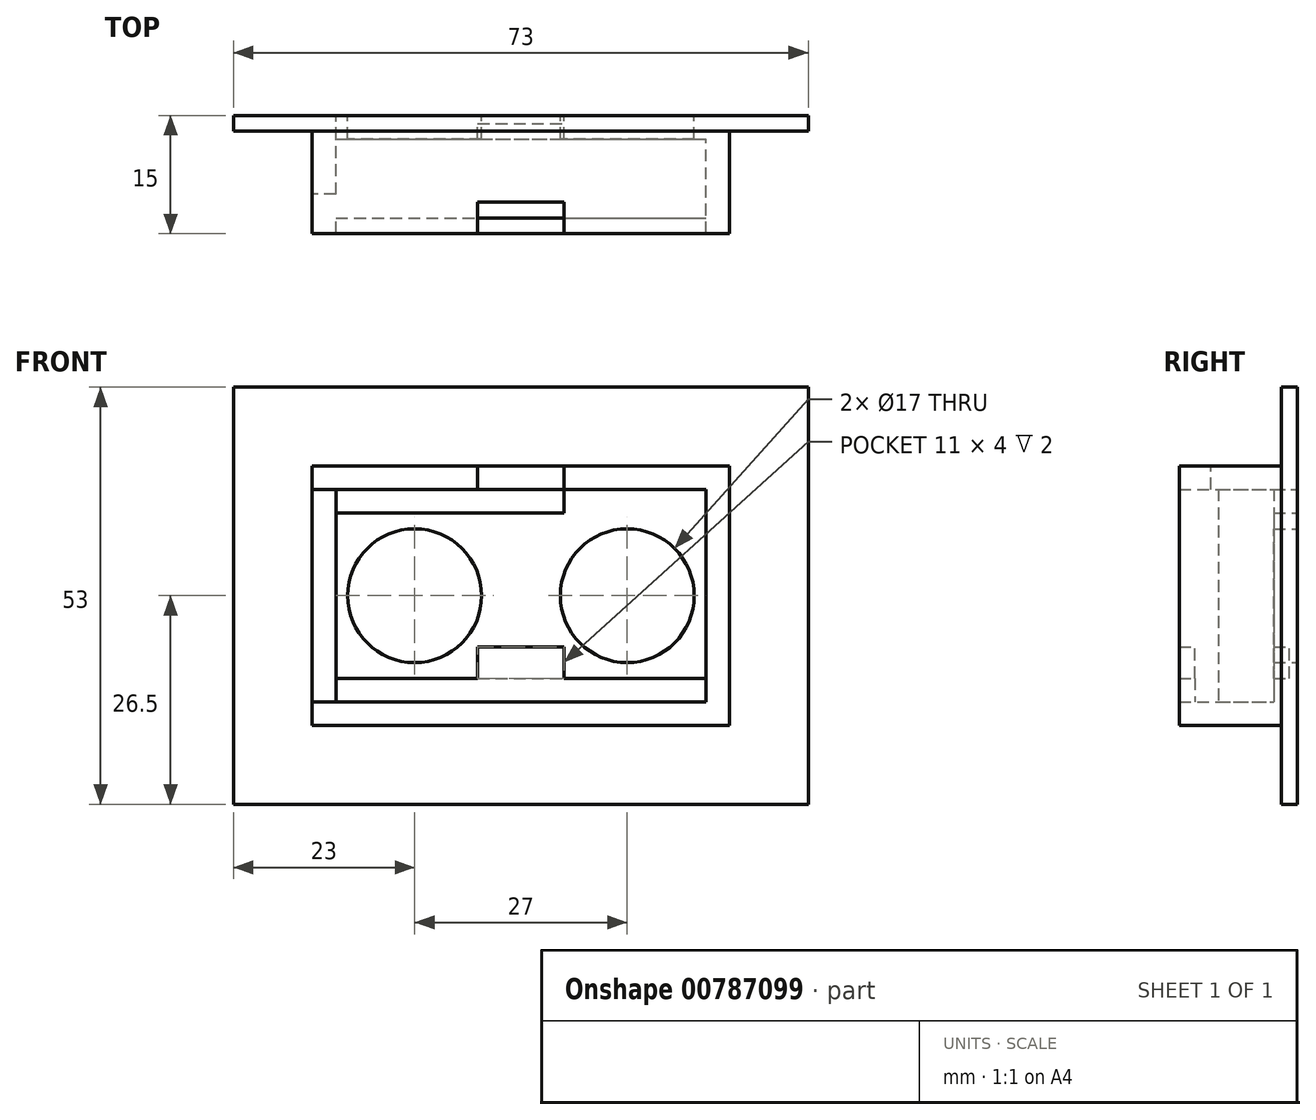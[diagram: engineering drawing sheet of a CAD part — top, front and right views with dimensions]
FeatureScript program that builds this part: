
annotation { "Feature Type Name" : "Feature", "Feature Type Description" : "" }
export const myFeature = defineFeature(function(context is Context, id is Id, definition is map)
    precondition{}
    {
        {
            var Q0;
            Q0=qCreatedBy(makeId("Front.planeOp"),FACE);
            var sketch = newSketch(context, id + "F0", { "sketchPlane" : qUnion([Q0])});
            skLineSegment(sketch, "E0.bottom", {"start": v(-23.5, 13.5) * mm, "end": v(23.5, 13.5) * mm});
            skLineSegment(sketch, "E0.top", {"start": v(-23.5, -13.5) * mm, "end": v(23.5, -13.5) * mm});
            skLineSegment(sketch, "E0.left", {"start": v(-23.5, 13.5) * mm, "end": v(-23.5, -13.5) * mm});
            skLineSegment(sketch, "E0.right", {"start": v(23.5, 13.5) * mm, "end": v(23.5, -13.5) * mm});
            skPoint(sketch, "E0.middle", {"position": v(0, 0) * mm});
            skPoint(sketch, "E1", {"position": v(-13.5, 0) * mm});
            skCircle(sketch, "E2", {"center": v(-13.5, 0) * mm, "radius": 8.5 * mm});
            skCircle(sketch, "E3.MirrorC", {"center": v(13.5, 0) * mm, "radius": 8.5 * mm});
            skPoint(sketch, "E4.positionSnap0", {"position": v(0, -13.5) * mm});
            skLineSegment(sketch, "E5.bottom", {"start": v(-5.5, -10.5) * mm, "end": v(5.5, -10.5) * mm});
            skLineSegment(sketch, "E5.top", {"start": v(-5.5, -6.5) * mm, "end": v(5.5, -6.5) * mm});
            skLineSegment(sketch, "E5.left", {"start": v(-5.5, -10.5) * mm, "end": v(-5.5, -6.5) * mm});
            skLineSegment(sketch, "E5.right", {"start": v(5.5, -10.5) * mm, "end": v(5.5, -6.5) * mm});
            skLineSegment(sketch, "E6.bottom", {"start": v(-23.5, 13.5) * mm, "end": v(-26.5, 13.5) * mm});
            skLineSegment(sketch, "E6.top", {"start": v(-23.5, -13.5) * mm, "end": v(-26.5, -13.5) * mm});
            skLineSegment(sketch, "E6.right", {"start": v(-26.5, 13.5) * mm, "end": v(-26.5, -13.5) * mm});
            skLineSegment(sketch, "E7.bottom", {"start": v(23.5, 13.5) * mm, "end": v(26.5, 13.5) * mm});
            skLineSegment(sketch, "E7.top", {"start": v(23.5, -13.5) * mm, "end": v(26.5, -13.5) * mm});
            skLineSegment(sketch, "E7.right", {"start": v(26.5, 13.5) * mm, "end": v(26.5, -13.5) * mm});
            skLineSegment(sketch, "E8.bottom", {"start": v(-26.5, 13.5) * mm, "end": v(26.5, 13.5) * mm});
            skLineSegment(sketch, "E8.top", {"start": v(-26.5, 16.5) * mm, "end": v(26.5, 16.5) * mm});
            skLineSegment(sketch, "E8.left", {"start": v(-26.5, 13.5) * mm, "end": v(-26.5, 16.5) * mm});
            skLineSegment(sketch, "E8.right", {"start": v(26.5, 13.5) * mm, "end": v(26.5, 16.5) * mm});
            skLineSegment(sketch, "E9.bottom", {"start": v(-26.5, -13.5) * mm, "end": v(26.5, -13.5) * mm});
            skLineSegment(sketch, "E9.top", {"start": v(-26.5, -16.5) * mm, "end": v(26.5, -16.5) * mm});
            skLineSegment(sketch, "E9.left", {"start": v(-26.5, -13.5) * mm, "end": v(-26.5, -16.5) * mm});
            skLineSegment(sketch, "E9.right", {"start": v(26.5, -13.5) * mm, "end": v(26.5, -16.5) * mm});
            skLineSegment(sketch, "E10.bottom", {"start": v(-5.5, -13.5) * mm, "end": v(5.5, -13.5) * mm});
            skLineSegment(sketch, "E10.top", {"start": v(-5.5, -16.5) * mm, "end": v(5.5, -16.5) * mm});
            skLineSegment(sketch, "E10.left", {"start": v(-5.5, -13.5) * mm, "end": v(-5.5, -16.5) * mm});
            skLineSegment(sketch, "E10.right", {"start": v(5.5, -13.5) * mm, "end": v(5.5, -16.5) * mm});
            skLineSegment(sketch, "E11.bottom", {"start": v(-5.5, 13.5) * mm, "end": v(5.5, 13.5) * mm});
            skLineSegment(sketch, "E11.top", {"start": v(-5.5, 16.5) * mm, "end": v(5.5, 16.5) * mm});
            skLineSegment(sketch, "E11.left", {"start": v(-5.5, 13.5) * mm, "end": v(-5.5, 16.5) * mm});
            skLineSegment(sketch, "E11.right", {"start": v(5.5, 13.5) * mm, "end": v(5.5, 16.5) * mm});
            skLineSegment(sketch, "E12.bottom", {"start": v(-26.5, 16.5) * mm, "end": v(-36.5, 16.5) * mm});
            skLineSegment(sketch, "E12.top", {"start": v(-26.5, -16.5) * mm, "end": v(-36.5, -16.5) * mm});
            skLineSegment(sketch, "E12.left", {"start": v(-26.5, 16.5) * mm, "end": v(-26.5, -16.5) * mm});
            skLineSegment(sketch, "E12.right", {"start": v(-36.5, 16.5) * mm, "end": v(-36.5, -16.5) * mm});
            skLineSegment(sketch, "E13.bottom", {"start": v(26.5, 16.5) * mm, "end": v(36.5, 16.5) * mm});
            skLineSegment(sketch, "E13.top", {"start": v(26.5, -16.5) * mm, "end": v(36.5, -16.5) * mm});
            skLineSegment(sketch, "E13.left", {"start": v(26.5, 16.5) * mm, "end": v(26.5, -16.5) * mm});
            skLineSegment(sketch, "E13.right", {"start": v(36.5, 16.5) * mm, "end": v(36.5, -16.5) * mm});
            skLineSegment(sketch, "E14.bottom", {"start": v(-36.5, -16.5) * mm, "end": v(36.5, -16.5) * mm});
            skLineSegment(sketch, "E14.top", {"start": v(-36.5, -26.5) * mm, "end": v(36.5, -26.5) * mm});
            skLineSegment(sketch, "E14.left", {"start": v(-36.5, -16.5) * mm, "end": v(-36.5, -26.5) * mm});
            skLineSegment(sketch, "E14.right", {"start": v(36.5, -16.5) * mm, "end": v(36.5, -26.5) * mm});
            skLineSegment(sketch, "E15.bottom", {"start": v(-36.5, 16.5) * mm, "end": v(36.5, 16.5) * mm});
            skLineSegment(sketch, "E15.top", {"start": v(-36.5, 26.5) * mm, "end": v(36.5, 26.5) * mm});
            skLineSegment(sketch, "E15.left", {"start": v(-36.5, 16.5) * mm, "end": v(-36.5, 26.5) * mm});
            skLineSegment(sketch, "E15.right", {"start": v(36.5, 16.5) * mm, "end": v(36.5, 26.5) * mm});
            skLineSegment(sketch, "E16.bottom", {"start": v(-26.5, 13.5) * mm, "end": v(-23.5, 13.5) * mm});
            skLineSegment(sketch, "E16.top", {"start": v(-26.5, 10.5) * mm, "end": v(-23.5, 10.5) * mm});
            skLineSegment(sketch, "E16.left", {"start": v(-26.5, 13.5) * mm, "end": v(-26.5, 10.5) * mm});
            skLineSegment(sketch, "E16.right", {"start": v(-23.5, 13.5) * mm, "end": v(-23.5, 10.5) * mm});
            skLineSegment(sketch, "E17.bottom", {"start": v(-26.5, -13.5) * mm, "end": v(-23.5, -13.5) * mm});
            skLineSegment(sketch, "E17.top", {"start": v(-26.5, -13.5) * mm, "end": v(-23.5, -13.5) * mm});
            skLineSegment(sketch, "E17.left", {"start": v(-26.5, -13.5) * mm, "end": v(-26.5, -13.5) * mm});
            skLineSegment(sketch, "E17.right", {"start": v(-23.5, -13.5) * mm, "end": v(-23.5, -13.5) * mm});
            skLineSegment(sketch, "E18.top", {"start": v(-26.5, -10.5) * mm, "end": v(-23.5, -10.5) * mm});
            skLineSegment(sketch, "E18.left", {"start": v(-26.5, -13.5) * mm, "end": v(-26.5, -10.5) * mm});
            skLineSegment(sketch, "E18.right", {"start": v(-23.5, -13.5) * mm, "end": v(-23.5, -10.5) * mm});
            skLineSegment(sketch, "E19.top", {"start": v(-23.5, 10.5) * mm, "end": v(23.5, 10.5) * mm});
            skLineSegment(sketch, "E19.right", {"start": v(23.5, 13.5) * mm, "end": v(23.5, 10.5) * mm});
            skLineSegment(sketch, "E20.bottom", {"start": v(-23.5, -10.5) * mm, "end": v(23.5, -10.5) * mm});
            skLineSegment(sketch, "E20.left", {"start": v(-23.5, -10.5) * mm, "end": v(-23.5, -13.5) * mm});
            skLineSegment(sketch, "E20.right", {"start": v(23.5, -10.5) * mm, "end": v(23.5, -13.5) * mm});
            skLineSegment(sketch, "E21.top", {"start": v(-5.5, 10.5) * mm, "end": v(5.5, 10.5) * mm});
            skLineSegment(sketch, "E21.left", {"start": v(-5.5, 13.5) * mm, "end": v(-5.5, 10.5) * mm});
            skLineSegment(sketch, "E21.right", {"start": v(5.5, 13.5) * mm, "end": v(5.5, 10.5) * mm});
            skSolve(sketch);
        }
        {
            var Q0;
            Q0=makeQuery(id+"F0.imprint","IMPRINT",FACE,{"disambiguationData":[TD([[makeQuery(id+"F0.imprint","IMPRINT",EDGE,{"derivedFrom":sQuery(id+"F0.wireOp",EDGE,"E2")}),-1.0]])]});
            var Q1;
            {var subQ13=sQuery(id+"F0.wireOp",EDGE,"E5.bottom");Q1=makeQuery(id+"F0.imprint","IMPRINT",FACE,{"disambiguationData":[TD([[makeQuery(id+"F0.imprint","IMPRINT",EDGE,{"derivedFrom":subQ13}),-1.0]])]});}
            var Q2;
            {var subQ1=sQuery(id+"F0.wireOp",EDGE,"E5.top");Q2=makeQuery(id+"F0.imprint","IMPRINT",FACE,{"disambiguationData":[TD([[makeQuery(id+"F0.imprint","IMPRINT",EDGE,{"derivedFrom":subQ1}),1.0]])]});}
            var Q3;
            {var subQ5=sQuery(id+"F0.wireOp",EDGE,"E0.right");Q3=makeQuery(id+"F0.imprint","IMPRINT",FACE,{"disambiguationData":[TD([[makeQuery(id+"F0.imprint","IMPRINT",EDGE,{"derivedFrom":subQ5}),-1.0]])]});}
            var Q4;
            {var subQ3=sQuery(id+"F0.wireOp",EDGE,"E16.right");Q4=makeQuery(id+"F0.imprint","IMPRINT",FACE,{"disambiguationData":[TD([[makeQuery(id+"F0.imprint","IMPRINT",EDGE,{"derivedFrom":subQ3}),1.0]])]});}
            var Q5;
            Q5=makeQuery(id+"F0.imprint","IMPRINT",FACE,{"disambiguationData":[TD([[makeQuery(id+"F0.imprint","IMPRINT",EDGE,{"derivedFrom":sQuery(id+"F0.wireOp",EDGE,"E11.bottom")}),-1.0]])]});
            var Q6;
            {var subQ4=sQuery(id+"F0.wireOp",EDGE,"E19.right");Q6=makeQuery(id+"F0.imprint","IMPRINT",FACE,{"disambiguationData":[TD([[makeQuery(id+"F0.imprint","IMPRINT",EDGE,{"derivedFrom":subQ4}),-1.0]])]});}
            var Q7;
            {var subQ2=sQuery(id+"F0.wireOp",EDGE,"E20.left");Q7=makeQuery(id+"F0.imprint","IMPRINT",FACE,{"disambiguationData":[TD([[makeQuery(id+"F0.imprint","IMPRINT",EDGE,{"derivedFrom":subQ2}),1.0]])]});}
            extrude(context, id + "F1", {"entities" : qUnion([Q0, Q1, Q2, Q3, Q4, Q5, Q6, Q7]), "depth" : 3 * mm, "offsetDistance" : 25 * mm});
        }
        {
            var Q0;
            Q0=makeQuery(id+"F0.imprint","IMPRINT",FACE,{"disambiguationData":[TD([[makeQuery(id+"F0.imprint","IMPRINT",EDGE,{"derivedFrom":sQuery(id+"F0.wireOp",EDGE,"E5.bottom")}),1.0]])]});
            var Q1;
            {var subQ0=sQuery(id+"F0.wireOp",EDGE,"E5.top");Q1=makeQuery(id+"F0.imprint","IMPRINT",FACE,{"disambiguationData":[TD([[makeQuery(id+"F0.imprint","IMPRINT",EDGE,{"derivedFrom":subQ0}),-1.0]])]});}
            extrude(context, id + "F2", {"entities" : qUnion([Q0, Q1]), "operationType" : NewBodyOperationType.ADD, "depth" : 1 * mm, "offsetDistance" : 25 * mm});
        }
        {
            var Q0;
            {var subQ5=sQuery(id+"F0.wireOp",EDGE,"E11.left");Q0=makeQuery(id+"F0.imprint","IMPRINT",FACE,{"disambiguationData":[TD([[makeQuery(id+"F0.imprint","IMPRINT",EDGE,{"derivedFrom":subQ5}),1.0]])]});}
            var Q1;
            {var subQ5=sQuery(id+"F0.wireOp",EDGE,"E11.right");Q1=makeQuery(id+"F0.imprint","IMPRINT",FACE,{"disambiguationData":[TD([[makeQuery(id+"F0.imprint","IMPRINT",EDGE,{"derivedFrom":subQ5}),-1.0]])]});}
            var Q2;
            {var subQ0=sQuery(id+"F0.wireOp",EDGE,"E0.right");Q2=makeQuery(id+"F0.imprint","IMPRINT",FACE,{"disambiguationData":[TD([[makeQuery(id+"F0.imprint","IMPRINT",EDGE,{"derivedFrom":subQ0}),1.0]])]});}
            var Q3;
            {var subQ5=sQuery(id+"F0.wireOp",EDGE,"E10.right");Q3=makeQuery(id+"F0.imprint","IMPRINT",FACE,{"disambiguationData":[TD([[makeQuery(id+"F0.imprint","IMPRINT",EDGE,{"derivedFrom":subQ5}),1.0]])]});}
            var Q4;
            Q4=makeQuery(id+"F0.imprint","IMPRINT",FACE,{"disambiguationData":[TD([[makeQuery(id+"F0.imprint","IMPRINT",EDGE,{"derivedFrom":sQuery(id+"F0.wireOp",EDGE,"E10.bottom")}),-1.0]])]});
            var Q5;
            {var subQ6=sQuery(id+"F0.wireOp",EDGE,"E10.left");Q5=makeQuery(id+"F0.imprint","IMPRINT",FACE,{"disambiguationData":[TD([[makeQuery(id+"F0.imprint","IMPRINT",EDGE,{"derivedFrom":subQ6}),-1.0]])]});}
            var Q6;
            {var subQ0=sQuery(id+"F0.wireOp",EDGE,"E10.left");Q6=makeQuery(id+"F0.imprint","IMPRINT",FACE,{"disambiguationData":[TD([[makeQuery(id+"F0.imprint","IMPRINT",EDGE,{"derivedFrom":subQ0}),1.0]])]});}
            extrude(context, id + "F3", {"entities" : qUnion([Q0, Q1, Q2, Q3, Q4, Q5, Q6]), "operationType" : NewBodyOperationType.ADD, "depth" : 15 * mm, "offsetDistance" : 25 * mm});
        }
        {
            var Q0;
            Q0=makeQuery(id+"F0.imprint","IMPRINT",FACE,{"disambiguationData":[TD([[makeQuery(id+"F0.imprint","IMPRINT",EDGE,{"derivedFrom":sQuery(id+"F0.wireOp",EDGE,"E11.bottom")}),1.0]])]});
            var Q1;
            {var subQ0=sQuery(id+"F0.wireOp",EDGE,"E11.left");Q1=makeQuery(id+"F0.imprint","IMPRINT",FACE,{"disambiguationData":[TD([[makeQuery(id+"F0.imprint","IMPRINT",EDGE,{"derivedFrom":subQ0}),-1.0]])]});}
            extrude(context, id + "F4", {"entities" : qUnion([Q0, Q1]), "operationType" : NewBodyOperationType.ADD, "depth" : 11 * mm, "offsetDistance" : 25 * mm});
        }
        {
            var Q0;
            Q0=makeQuery(id+"F0.imprint","IMPRINT",FACE,{"disambiguationData":[TD([[makeQuery(id+"F0.imprint","IMPRINT",EDGE,{"derivedFrom":sQuery(id+"F0.wireOp",EDGE,"E15.top")}),-1.0]])]});
            var Q1;
            {var subQ0=sQuery(id+"F0.wireOp",EDGE,"E12.right");Q1=makeQuery(id+"F0.imprint","IMPRINT",FACE,{"disambiguationData":[TD([[makeQuery(id+"F0.imprint","IMPRINT",EDGE,{"derivedFrom":subQ0}),1.0]])]});}
            var Q2;
            Q2=makeQuery(id+"F0.imprint","IMPRINT",FACE,{"disambiguationData":[TD([[makeQuery(id+"F0.imprint","IMPRINT",EDGE,{"derivedFrom":sQuery(id+"F0.wireOp",EDGE,"E14.top")}),1.0]])]});
            var Q3;
            {var subQ0=sQuery(id+"F0.wireOp",EDGE,"E13.right");Q3=makeQuery(id+"F0.imprint","IMPRINT",FACE,{"disambiguationData":[TD([[makeQuery(id+"F0.imprint","IMPRINT",EDGE,{"derivedFrom":subQ0}),-1.0]])]});}
            extrude(context, id + "F5", {"entities" : qUnion([Q0, Q1, Q2, Q3]), "operationType" : NewBodyOperationType.ADD, "depth" : 2 * mm, "offsetDistance" : 25 * mm});
        }
        {
            var Q0;
            Q0=makeQuery(id+"F0.imprint","IMPRINT",FACE,{"disambiguationData":[TD([[makeQuery(id+"F0.imprint","IMPRINT",EDGE,{"derivedFrom":sQuery(id+"F0.wireOp",EDGE,"E16.bottom")}),-1.0]])]});
            var Q1;
            Q1=makeQuery(id+"F0.imprint","IMPRINT",FACE,{"disambiguationData":[TD([[makeQuery(id+"F0.imprint","IMPRINT",EDGE,{"derivedFrom":sQuery(id+"F0.wireOp",EDGE,"E0.left")}),-1.0]])]});
            var Q2;
            Q2=makeQuery(id+"F0.imprint","IMPRINT",FACE,{"disambiguationData":[TD([[makeQuery(id+"F0.imprint","IMPRINT",EDGE,{"derivedFrom":sQuery(id+"F0.wireOp",EDGE,"E17.bottom")}),1.0]])]});
            extrude(context, id + "F6", {"entities" : qUnion([Q0, Q1, Q2]), "operationType" : NewBodyOperationType.ADD, "depth" : 10 * mm, "offsetDistance" : 25 * mm});
        }
        {
            var Q0;
            Q0=makeQuery(id+"F0.imprint","IMPRINT",FACE,{"disambiguationData":[TD([[makeQuery(id+"F0.imprint","IMPRINT",EDGE,{"derivedFrom":sQuery(id+"F0.wireOp",EDGE,"E16.bottom")}),-1.0]])]});
            var Q1;
            Q1=makeQuery(id+"F0.imprint","IMPRINT",FACE,{"disambiguationData":[TD([[makeQuery(id+"F0.imprint","IMPRINT",EDGE,{"derivedFrom":sQuery(id+"F0.wireOp",EDGE,"E17.bottom")}),1.0]])]});
            var Q2;
            {var subQ3=sQuery(id+"F0.wireOp",EDGE,"E16.right");Q2=makeQuery(id+"F0.imprint","IMPRINT",FACE,{"disambiguationData":[TD([[makeQuery(id+"F0.imprint","IMPRINT",EDGE,{"derivedFrom":subQ3}),1.0]])]});}
            var Q3;
            {var subQ13=sQuery(id+"F0.wireOp",EDGE,"E5.bottom");Q3=makeQuery(id+"F0.imprint","IMPRINT",FACE,{"disambiguationData":[TD([[makeQuery(id+"F0.imprint","IMPRINT",EDGE,{"derivedFrom":subQ13}),-1.0]])]});}
            var Q4;
            {var subQ0=sQuery(id+"F0.wireOp",EDGE,"E5.bottom");Q4=makeQuery(id+"F0.imprint","IMPRINT",FACE,{"disambiguationData":[TD([[makeQuery(id+"F0.imprint","IMPRINT",EDGE,{"derivedFrom":subQ0}),1.0]])]});}
            var Q5;
            {var subQ4=sQuery(id+"F0.wireOp",EDGE,"E19.right");Q5=makeQuery(id+"F0.imprint","IMPRINT",FACE,{"disambiguationData":[TD([[makeQuery(id+"F0.imprint","IMPRINT",EDGE,{"derivedFrom":subQ4}),-1.0]])]});}
            var Q6;
            {var subQ2=sQuery(id+"F0.wireOp",EDGE,"E20.left");Q6=makeQuery(id+"F0.imprint","IMPRINT",FACE,{"disambiguationData":[TD([[makeQuery(id+"F0.imprint","IMPRINT",EDGE,{"derivedFrom":subQ2}),1.0]])]});}
            extrude(context, id + "F7", {"entities" : qUnion([Q0, Q1, Q2, Q3, Q4, Q5, Q6]), "depth" : 15 * mm, "offsetDistance" : 25 * mm, "hasSecondDirection" : true, "secondDirectionOppositeDirection" : false, "secondDirectionDepth" : 13 * mm});
        }
    });
